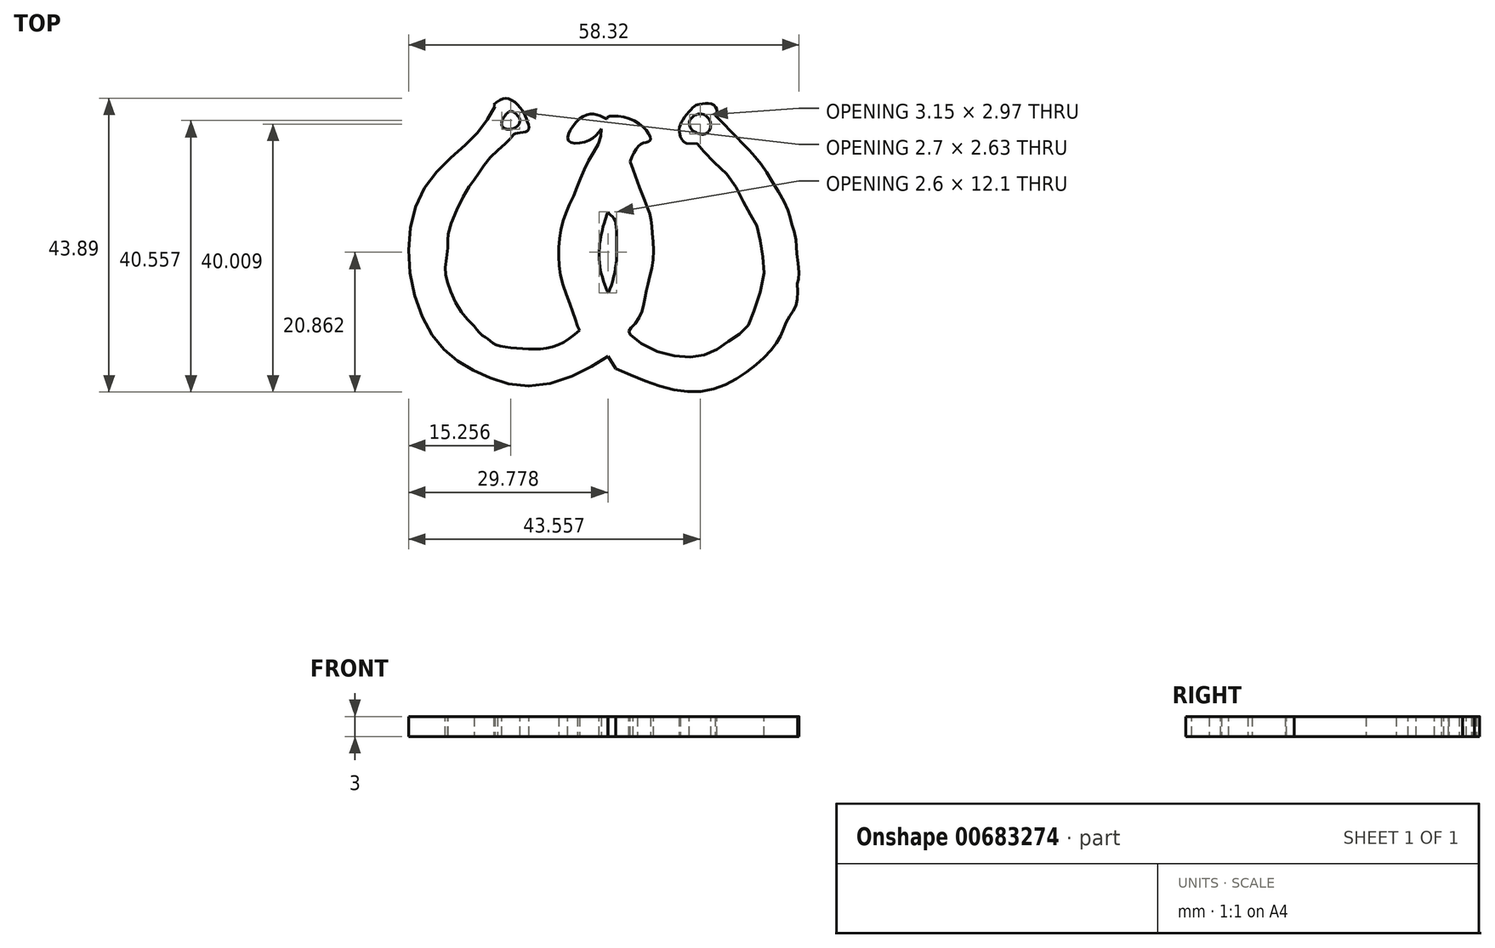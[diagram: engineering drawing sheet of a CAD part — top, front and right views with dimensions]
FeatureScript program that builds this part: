
annotation { "Feature Type Name" : "Feature", "Feature Type Description" : "" }
export const myFeature = defineFeature(function(context is Context, id is Id, definition is map)
    precondition{}
    {
        {
            var Q0;
            Q0=qCreatedBy(makeId("Top.planeOp"),FACE);
            var sketch = newSketch(context, id + "F0", { "sketchPlane" : qUnion([Q0])});
            skFitSpline(sketch, "E0", {"points": [v(-58.65, 48.83) * mm, v(-56.84, 49.79) * mm, v(-54.73, 48.43) * mm, v(-53.68, 46.47) * mm, v(-53.48, 45.02) * mm, v(-54.53, 44.67) * mm, v(-55.69, 44.36) * mm, v(-56.39, 43.46) * mm, v(-58.95, 41.2) * mm, v(-61.06, 38.34) * mm, v(-62.76, 35.88) * mm, v(-65.42, 29.7) * mm, v(-65.48, 27.95) * mm, v(-65.88, 24.44) * mm, v(-65.63, 22.63) * mm, v(-63.9, 18.47) * mm, v(-61.57, 15.77) * mm], "startDerivative": vector(30.85, 26.25) * mm, "endDerivative": vector(33.2, -31.46) * mm});
            skFitSpline(sketch, "E1", {"points": [v(35.39, 99.2) * mm, v(59.26, 113.54) * mm, v(128.03, 89.66) * mm], "startDerivative": vector(53.16, 52.04) * mm, "endDerivative": vector(126.37, -62.16) * mm});
            skFitSpline(sketch, "E2", {"points": [v(-61.57, 15.77) * mm, v(-60.41, 14.4) * mm, v(-59.46, 13.8) * mm, v(-58.54, 13.03) * mm, v(-56.06, 12.5) * mm, v(-52.3, 12.3) * mm, v(-48.62, 13.11) * mm, v(-45.07, 15.77) * mm, v(-43, 17.8) * mm, v(-41.72, 20.15) * mm, v(-40.45, 24.5) * mm, v(-40.31, 29.13) * mm, v(-40.72, 31.87) * mm, v(-41.59, 32.81) * mm, v(-39.44, 37.5) * mm, v(-36.7, 42.93) * mm, v(-35.29, 43.46) * mm, v(-37.5, 46.34) * mm, v(-41.79, 46.68) * mm, v(-40.58, 45.27) * mm, v(-42.26, 45.67) * mm, v(-42.66, 44.07) * mm, v(-44.67, 40.11) * mm, v(-46.48, 35.76) * mm, v(-48.22, 31.74) * mm, v(-48.89, 27.79) * mm, v(-48.69, 23.43) * mm, v(-47.08, 18.6) * mm, v(-46.14, 15.77) * mm], "startDerivative": vector(42.05, -57.94) * mm, "endDerivative": vector(23.28, -75.89) * mm});
            skFitSpline(sketch, "E3", {"points": [v(-41.59, 32.81) * mm, v(-42.52, 29.73) * mm, v(-42.86, 25.17) * mm, v(-41.72, 20.95) * mm], "startDerivative": vector(-3.43, -9.69) * mm, "endDerivative": vector(4.24, -11.8) * mm});
            skFitSpline(sketch, "E4", {"points": [v(-42.26, 45.67) * mm, v(-44.47, 43.46) * mm, v(-47.48, 43.46) * mm, v(-46.28, 46.28) * mm, v(-43.86, 47.42) * mm, v(-41.79, 46.68) * mm], "startDerivative": vector(-8.04, -12.22) * mm, "endDerivative": vector(11.49, -6.01) * mm});
            skFitSpline(sketch, "E5", {"points": [v(-37.8, 39.1) * mm, v(-37.2, 37.34) * mm], "startDerivative": vector(0.62, -1.75) * mm, "endDerivative": vector(0.62, -1.75) * mm});
            skFitSpline(sketch, "E6", {"points": [v(-37.2, 37.34) * mm, v(-36.3, 35.02) * mm, v(-35.3, 32.32) * mm, v(-34.96, 29.9) * mm, v(-34.82, 25.64) * mm, v(-35.68, 21.85) * mm, v(-36.2, 19.25) * mm, v(-37.2, 16.54) * mm, v(-38.42, 15.12) * mm, v(-38.28, 14.46) * mm, v(-35.49, 12.47) * mm, v(-31.22, 11.24) * mm, v(-27.95, 11.24) * mm, v(-25.35, 12.23) * mm, v(-23.03, 13.84) * mm, v(-21.08, 15.22) * mm, v(-19.8, 17.97) * mm, v(-18.29, 23.46) * mm, v(-18.62, 27.25) * mm, v(-19.33, 30.71) * mm, v(-20.56, 32.81) * mm, v(-22.27, 36.16) * mm, v(-24.45, 39.1) * mm, v(-27.24, 41.75) * mm, v(-28.14, 42.93) * mm, v(-29.9, 43.08) * mm, v(-30.8, 44.07) * mm], "startDerivative": vector(23.78, -62.96) * mm, "endDerivative": vector(-26.03, 48.46) * mm});
            skFitSpline(sketch, "E7", {"points": [v(-30.97, 45.1) * mm, v(-30.8, 44.07) * mm], "startDerivative": vector(0.18, -1.04) * mm, "endDerivative": vector(0.18, -1.04) * mm});
            skFitSpline(sketch, "E8", {"points": [v(-30.97, 45.1) * mm, v(-30.55, 46.34) * mm, v(-29.28, 48.01) * mm, v(-28.47, 48.73) * mm, v(-27.44, 48.95) * mm, v(-25.83, 48.8) * mm, v(-25.3, 47.75) * mm, v(-25.85, 46.9) * mm, v(-27.35, 45.27) * mm, v(-29.9, 43.08) * mm], "startDerivative": vector(2.73, 11.73) * mm, "endDerivative": vector(-16.76, -13.6) * mm});
            skFitSpline(sketch, "E9", {"points": [v(-25.57, 47.2) * mm, v(-24.27, 45.96) * mm, v(-22.19, 43.74) * mm, v(-19.7, 41.17) * mm, v(-17.4, 37.93) * mm, v(-14.83, 33.37) * mm, v(-14.18, 31.25) * mm, v(-13.5, 28.58) * mm, v(-13.35, 26.4) * mm, v(-13.05, 23.01) * mm, v(-13.31, 22.07) * mm], "startDerivative": vector(15.51, -14.32) * mm, "endDerivative": vector(-5.99, -12.66) * mm});
            skFitSpline(sketch, "E10", {"points": [v(-353.27, 126.16) * mm, v(-368.08, 148.12) * mm], "startDerivative": vector(-14.8, 21.97) * mm, "endDerivative": vector(-14.8, 21.97) * mm});
            skFitSpline(sketch, "E11", {"points": [v(-13.31, 22.07) * mm, v(-13.5, 18.85) * mm, v(-14.69, 16.83) * mm, v(-16, 13.9) * mm, v(-19.8, 9.7) * mm, v(-27.95, 5.93) * mm, v(-40.45, 9.39) * mm], "startDerivative": vector(1.5, -27.45) * mm, "endDerivative": vector(-50.97, 22.05) * mm});
            skFitSpline(sketch, "E12", {"points": [v(-38.28, 14.46) * mm, v(-41.59, 11.24) * mm, v(-52.26, 6.83) * mm, v(-61.57, 9.09) * mm, v(-67.9, 14.46) * mm, v(-71.36, 26.39) * mm, v(-68.35, 37.34) * mm, v(-61.57, 44.07) * mm, v(-58.07, 49.32) * mm], "startDerivative": vector(-28.85, -34.47) * mm, "endDerivative": vector(27.42, 51.15) * mm});
            skFitSpline(sketch, "E13", {"points": [v(-58.65, 48.83) * mm, v(-55.69, 44.36) * mm], "startDerivative": vector(2.96, -4.47) * mm, "endDerivative": vector(2.96, -4.47) * mm});
            skFitSpline(sketch, "E14", {"points": [v(-37.8, 39.1) * mm, v(-38.3, 40.29) * mm], "startDerivative": vector(-0.49, 1.2) * mm, "endDerivative": vector(-0.49, 1.2) * mm});
            skFitSpline(sketch, "E15", {"points": [v(-41.72, 20.95) * mm, v(-41.5, 20.71) * mm], "startDerivative": vector(0.22, -0.24) * mm, "endDerivative": vector(0.22, -0.24) * mm});
            skFitSpline(sketch, "E16", {"points": [v(-40.45, 9.39) * mm, v(-41.59, 11.24) * mm], "startDerivative": vector(-1.14, 1.85) * mm, "endDerivative": vector(-1.14, 1.85) * mm});
            skFitSpline(sketch, "E17", {"points": [v(-46.14, 15.77) * mm, v(-45.8, 15.12) * mm], "startDerivative": vector(0.34, -0.64) * mm, "endDerivative": vector(0.34, -0.64) * mm});
            skFitSpline(sketch, "E18", {"points": [v(-41.79, 46.68) * mm, v(-42.58, 45.2) * mm], "startDerivative": vector(-0.8, -1.49) * mm, "endDerivative": vector(-0.8, -1.49) * mm});
            skFitSpline(sketch, "E19", {"points": [v(-27.63, 47.42) * mm, v(-29.25, 46.68) * mm, v(-29.12, 45.2) * mm, v(-27, 44.5) * mm, v(-26.27, 46.18) * mm, v(-27.63, 47.42) * mm]});
            skFitSpline(sketch, "E20", {"points": [v(-55.95, 47.8) * mm, v(-56.84, 47.34) * mm, v(-57.43, 45.67) * mm, v(-55.9, 45.2) * mm, v(-54.73, 46.47) * mm, v(-55.95, 47.8) * mm]});
            skSolve(sketch);
        }
        {
            var Q0;
            Q0 = qSketchRegion(id + "F0", true);
            extrude(context, id + "F1", {"entities" : qUnion([Q0]), "depth" : 3 * mm, "offsetDistance" : 25 * mm});
        }
    });
